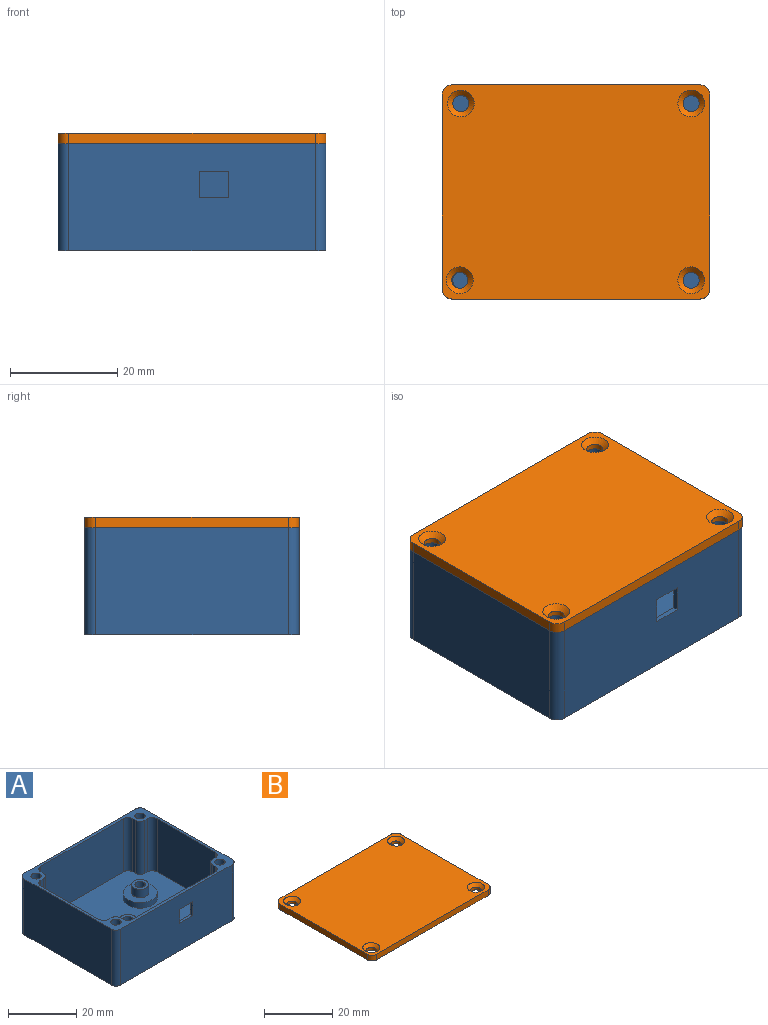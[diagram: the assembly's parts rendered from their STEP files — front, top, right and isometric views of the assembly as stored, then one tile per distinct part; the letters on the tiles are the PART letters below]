
ASSEMBLY  parts=2 mates=1
PART A: 57 faces, bbox 50x40x20 mm
  f0: plane 34x19mm, normal (0,1,0), area 618.8mm2, adj f2,f6,f37,f41,f53,f54,f55,f56
  f1: plane 46x20mm, normal (0,-1,0), area 892.8mm2, adj f6,f10,f50,f51,f53,f54,f55,f56
  f2: plane 48x38mm, normal (0,0,1), area 1563.5mm2, adj f0,f3,f4,f5,f11,f12,f13,f14
  f3: plane 24x19mm, normal (-1,0,0), area 456mm2, adj f2,f6,f39,f43
  f4: plane 24x19mm, normal (1,0,0), area 456mm2, adj f2,f6,f42,f48
  f5: plane 34x19mm, normal (0,-1,0), area 646mm2, adj f2,f6,f44,f46
  f6: plane 50x40mm, normal (0,0,1), area 247.7mm2, adj f0,f1,f3,f4,f5,f7,f8,f9
  f7: plane 46x20mm, normal (0,1,0), area 920mm2, adj f6,f10,f49,f52
  f8: plane 36x20mm, normal (-1,0,0), area 720mm2, adj f6,f10,f49,f50
  f9: plane 36x20mm, normal (1,0,0), area 720mm2, adj f6,f10,f51,f52
  f10: plane 50x40mm, normal (0,0,-1), area 1982.4mm2, adj f1,f7,f8,f9,f27,f30,f49,f50
  f11: plane 19x1mm, normal (0,-1,0), area 19mm2, adj f2,f6,f47,f48
  f12: plane 19x1mm, normal (1,0,0), area 19mm2, adj f2,f6,f46,f47
  f13: plane 19x1mm, normal (0,-1,0), area 19mm2, adj f2,f6,f43,f45
  f14: plane 19x1mm, normal (-1,0,0), area 19mm2, adj f2,f6,f44,f45
  f15: plane 19x1mm, normal (0,1,0), area 19mm2, adj f2,f6,f40,f42
  f16: plane 19x1mm, normal (1,0,0), area 19mm2, adj f2,f6,f40,f41
  f17: plane 19x1mm, normal (0,1,0), area 19mm2, adj f2,f6,f38,f39
  f18: plane 19x1mm, normal (-1,0,0), area 19mm2, adj f2,f6,f37,f38
  f19: cylinder r=1.5mm len=10mm, axis (0,0,1), area 94.2mm2, adj f6,f20
  f20: plane 3x3mm, normal (0,0,1), area 7.1mm2, adj f19
  f21: cylinder r=1.5mm len=10mm, axis (0,0,1), area 94.2mm2, adj f6,f22
  f22: plane 3x3mm, normal (0,0,1), area 7.1mm2, adj f21
  f23: cylinder r=1.5mm len=10mm, axis (0,0,1), area 94.2mm2, adj f6,f24
  f24: plane 3x3mm, normal (0,0,1), area 7.1mm2, adj f23
  f25: cylinder r=1.5mm len=10mm, axis (0,0,1), area 94.2mm2, adj f6,f26
  f26: plane 3x3mm, normal (0,0,1), area 7.1mm2, adj f25
  f27: cylinder r=1.5mm len=6mm, axis (0,0,-1), area 56.5mm2, adj f10,f29
  f28: cylinder r=2.5mm len=5mm, axis (0,0,-1), area 47.1mm2, adj f29,f36
  f29: plane 5x5mm, normal (0,0,1), area 12.6mm2, adj f27,f28
  f30: cylinder r=1.5mm len=6mm, axis (0,0,-1), area 56.5mm2, adj f10,f32
  f31: cylinder r=2.5mm len=5mm, axis (0,0,-1), area 47.1mm2, adj f32,f34
  f32: plane 5x5mm, normal (0,0,1), area 12.6mm2, adj f30,f31
  f33: cylinder r=5mm len=10mm, axis (0,0,-1), area 62.8mm2, adj f2,f34
  f34: plane 10x10mm, normal (0,0,1), area 58.9mm2, adj f31,f33
  f35: cylinder r=5mm len=10mm, axis (0,0,-1), area 62.8mm2, adj f2,f36
  f36: plane 10x10mm, normal (0,0,1), area 58.9mm2, adj f28,f35
  f37: cylinder r=2mm len=19mm, axis (0,0,1), area 59.7mm2, adj f0,f2,f6,f18
  f38: cylinder r=2mm len=19mm, axis (0,0,1), area 59.7mm2, adj f2,f6,f17,f18
  f39: cylinder r=2mm len=19mm, axis (0,0,1), area 59.7mm2, adj f2,f3,f6,f17
  f40: cylinder r=2mm len=19mm, axis (0,0,1), area 59.7mm2, adj f2,f6,f15,f16
  f41: cylinder r=2mm len=19mm, axis (0,0,-1), area 59.7mm2, adj f0,f2,f6,f16
  f42: cylinder r=2mm len=19mm, axis (0,0,1), area 59.7mm2, adj f2,f4,f6,f15
  f43: cylinder r=2mm len=19mm, axis (0,0,-1), area 59.7mm2, adj f2,f3,f6,f13
  f44: cylinder r=2mm len=19mm, axis (0,0,1), area 59.7mm2, adj f2,f5,f6,f14
  f45: cylinder r=2mm len=19mm, axis (0,0,1), area 59.7mm2, adj f2,f6,f13,f14
  f46: cylinder r=2mm len=19mm, axis (0,0,-1), area 59.7mm2, adj f2,f5,f6,f12
  f47: cylinder r=2mm len=19mm, axis (0,0,1), area 59.7mm2, adj f2,f6,f11,f12
  f48: cylinder r=2mm len=19mm, axis (0,0,-1), area 59.7mm2, adj f2,f4,f6,f11
  f49: cylinder r=2mm len=20mm, axis (0,0,1), area 62.8mm2, adj f6,f7,f8,f10
  f50: cylinder r=2mm len=20mm, axis (0,0,-1), area 62.8mm2, adj f1,f6,f8,f10
  f51: cylinder r=2mm len=20mm, axis (0,0,1), area 62.8mm2, adj f1,f6,f9,f10
  f52: cylinder r=2mm len=20mm, axis (0,0,-1), area 62.8mm2, adj f6,f7,f9,f10
  f53: plane 5.45x1mm, normal (0,0,-1), area 5.4mm2, adj f0,f1,f54,f56
  f54: plane 5x1mm, normal (1,0,0), area 5mm2, adj f0,f1,f53,f55
  f55: plane 5.45x1mm, normal (0,0,1), area 5.4mm2, adj f0,f1,f54,f56
  f56: plane 5x1mm, normal (-1,0,0), area 5mm2, adj f0,f1,f53,f55
PART B: 18 faces, bbox 50x40x2 mm
  f0: plane 46x2mm, normal (0,1,0), area 92mm2, adj f8,f9,f14,f17
  f1: plane 36x2mm, normal (-1,0,0), area 72mm2, adj f8,f9,f14,f15
  f2: plane 46x2mm, normal (0,-1,0), area 92mm2, adj f8,f9,f15,f16
  f3: cylinder r=1.5mm len=3mm, axis (0,0,-1), area 9.4mm2, adj f9,f10
  f4: cylinder r=1.5mm len=3mm, axis (0,0,-1), area 9.4mm2, adj f9,f11
  f5: cylinder r=1.5mm len=3mm, axis (0,0,-1), area 9.4mm2, adj f9,f12
  f6: cylinder r=1.5mm len=3mm, axis (0,0,-1), area 9.4mm2, adj f9,f13
  f7: plane 36x2mm, normal (1,0,0), area 72mm2, adj f8,f9,f16,f17
  f8: plane 50x40mm, normal (0,0,1), area 1918mm2, adj f0,f1,f2,f7,f10,f11,f12,f13
  f9: plane 50x40mm, normal (0,0,-1), area 1968.3mm2, adj f0,f1,f2,f3,f4,f5,f6,f7
  f10: cone r=1.5mm half-angle=45deg, axis (0,0,1), area 17.8mm2, adj f3,f8
  f11: cone r=1.5mm half-angle=45deg, axis (0,0,1), area 17.8mm2, adj f4,f8
  f12: cone r=1.5mm half-angle=45deg, axis (0,0,1), area 17.8mm2, adj f5,f8
  f13: cone r=1.5mm half-angle=45deg, axis (0,0,1), area 17.8mm2, adj f6,f8
  f14: cylinder r=2mm len=2mm, axis (0,0,1), area 6.3mm2, adj f0,f1,f8,f9
  f15: cylinder r=2mm len=2mm, axis (0,0,-1), area 6.3mm2, adj f1,f2,f8,f9
  f16: cylinder r=2mm len=2mm, axis (0,0,1), area 6.3mm2, adj f2,f7,f8,f9
  f17: cylinder r=2mm len=2mm, axis (0,0,-1), area 6.3mm2, adj f0,f7,f8,f9
PLACE A t=(-22.59,-23.12,11.1)mm fixed
PLACE B t=(-89.89,-25.69,31.1)mm
MATE slider A.f23 <-> B.f4  axis (0,0,1) through (-39.92,-7.61,31.1)mm
